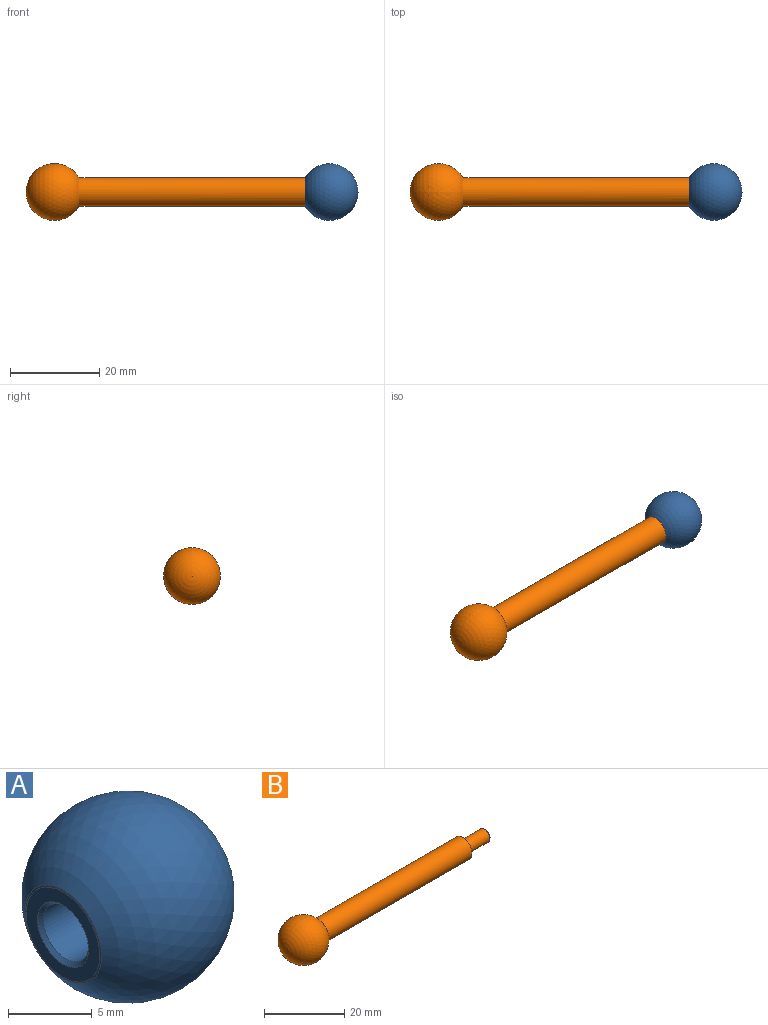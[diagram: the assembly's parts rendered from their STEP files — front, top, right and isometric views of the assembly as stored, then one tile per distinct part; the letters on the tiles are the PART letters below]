
ASSEMBLY  parts=2 mates=1
PART A: 7 faces, bbox 11.8x12.7x12.7 mm
  f0: plane 6.21x6.21mm, normal (-1,0,0), area 15.7mm2, adj f4,f6
  f1: cylinder r=1.91mm len=6.55mm, axis (-1,0,0), area 78.4mm2, adj f5,f6
  f2: plane 3.3x3.3mm, normal (-1,0,0), area 8.6mm2, adj f5
  f3: sphere r=6.35mm, area 471.4mm2, adj f4
  f4: cone r=3.11mm half-angle=74.7deg, axis (1,0,0), area 2.7mm2, adj f0,f3
  f5: cone r=1.65mm half-angle=45deg, axis (-1,0,0), area 4mm2, adj f1,f2
  f6: cone r=1.91mm half-angle=45deg, axis (-1,0,0), area 4.6mm2, adj f0,f1
PART B: 8 faces, bbox 70.3x12.7x12.7 mm
  f0: plane 3.53x3.53mm, normal (1,0,0), area 9.8mm2, adj f6
  f1: sphere r=6.35mm, area 472.8mm2, adj f2
  f2: cylinder r=3.17mm len=50.67mm, axis (1,0,0), area 1010.9mm2, adj f1,f5
  f3: cylinder r=1.89mm len=7.37mm, axis (1,0,0), area 87.6mm2, adj f6,f7
  f4: plane 6.1x6.1mm, normal (1,0,0), area 16.4mm2, adj f5,f7
  f5: cone r=3.05mm half-angle=45deg, axis (-1,0,0), area 3.5mm2, adj f2,f4
  f6: cone r=1.77mm half-angle=45deg, axis (-1,0,0), area 2.1mm2, adj f0,f3
  f7: torus R=2.02mm, axis (1,0,0), area 2.4mm2, adj f3,f4
PLACE A rot(axis=(1,0,0),19.9deg) t=(60.85,10.61,3.84)mm
PLACE B t=(10.86,10.61,0.66)mm fixed
MATE cylindrical B.f2 <-> A.f1  axis (1,0,0) through (69.28,10.61,3.84)mm
